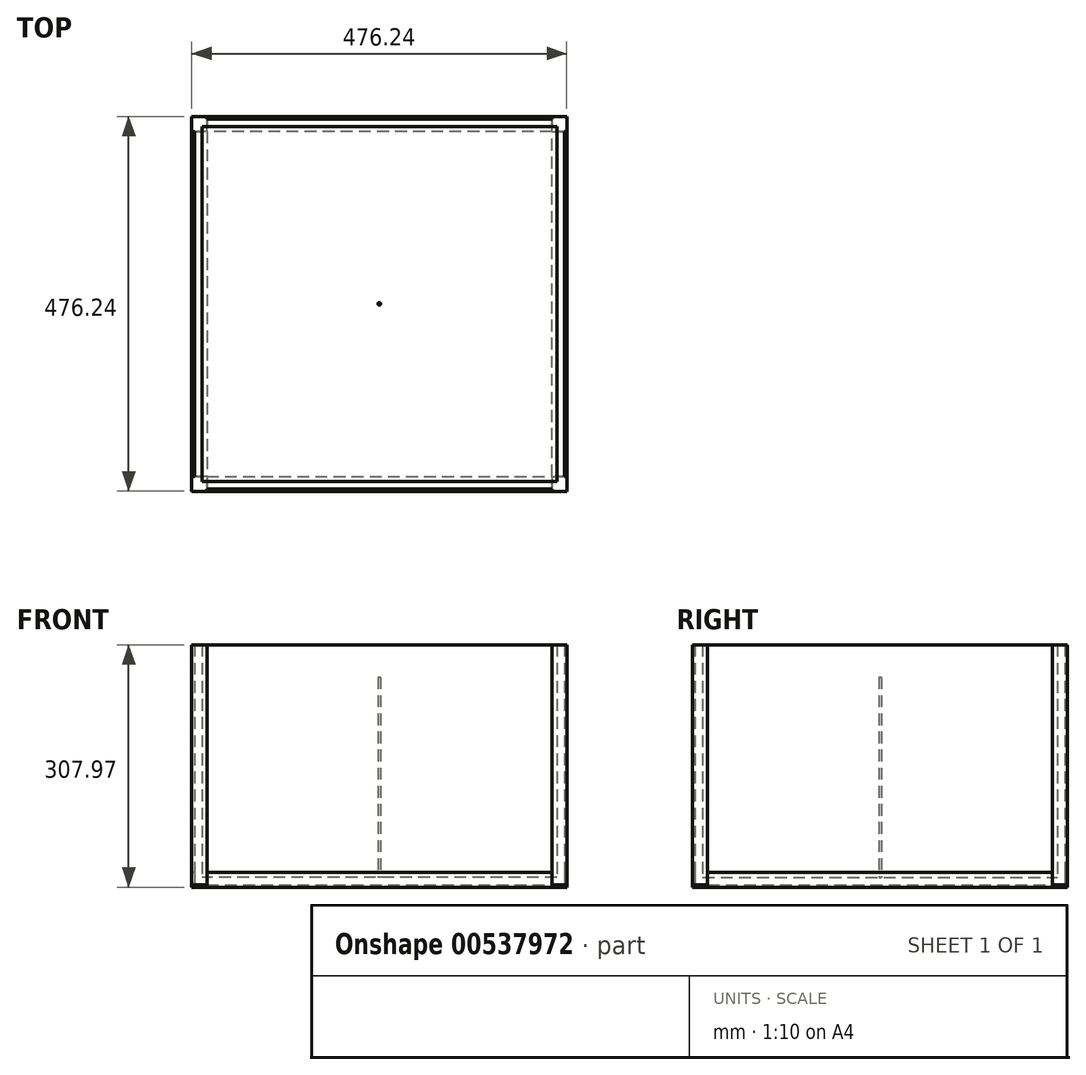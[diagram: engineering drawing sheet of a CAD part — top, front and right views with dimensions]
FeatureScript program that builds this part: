
annotation { "Feature Type Name" : "Feature", "Feature Type Description" : "" }
export const myFeature = defineFeature(function(context is Context, id is Id, definition is map)
    precondition{}
    {
        {
            var Q0;
            Q0=qCreatedBy(makeId("Top.planeOp"),FACE);
            var sketch = newSketch(context, id + "F0", { "sketchPlane" : qUnion([Q0])});
            skLineSegment(sketch, "E0.bottom", {"start": v(234.95, -234.95) * mm, "end": v(-234.95, -234.95) * mm});
            skLineSegment(sketch, "E0.top", {"start": v(234.95, 234.95) * mm, "end": v(-234.95, 234.95) * mm});
            skLineSegment(sketch, "E0.left", {"start": v(234.95, -234.95) * mm, "end": v(234.95, 234.95) * mm});
            skLineSegment(sketch, "E0.right", {"start": v(-234.95, -234.95) * mm, "end": v(-234.95, 234.95) * mm});
            skPoint(sketch, "E0.middle", {"position": v(0, 0) * mm});
            skLineSegment(sketch, "E1", {"start": v(-234.95, 234.95) * mm, "end": v(-234.95, 238.13) * mm});
            skLineSegment(sketch, "E2", {"start": v(-234.95, 238.13) * mm, "end": v(-238.13, 238.13) * mm});
            skLineSegment(sketch, "E3", {"start": v(-238.13, 238.13) * mm, "end": v(-238.13, 219.08) * mm});
            skLineSegment(sketch, "E4", {"start": v(-238.13, 219.08) * mm, "end": v(-234.95, 219.08) * mm});
            skLineSegment(sketch, "E5", {"start": v(-238.13, 238.13) * mm, "end": v(-219.08, 238.13) * mm});
            skLineSegment(sketch, "E6", {"start": v(-219.08, 238.13) * mm, "end": v(-219.08, 234.95) * mm});
            skLineSegment(sketch, "E7.1.0", {"start": v(-238.13, -238.13) * mm, "end": v(-219.08, -238.13) * mm});
            skLineSegment(sketch, "E7.1.1", {"start": v(-219.08, -238.13) * mm, "end": v(-219.08, -234.95) * mm});
            skLineSegment(sketch, "E7.1.2", {"start": v(-238.13, -238.13) * mm, "end": v(-238.13, -219.08) * mm});
            skLineSegment(sketch, "E7.1.3", {"start": v(-238.13, -219.08) * mm, "end": v(-234.95, -219.08) * mm});
            skLineSegment(sketch, "E7.1.4", {"start": v(-238.13, -234.95) * mm, "end": v(-238.13, -238.13) * mm});
            skLineSegment(sketch, "E7.1.5", {"start": v(-234.95, -234.95) * mm, "end": v(-238.13, -234.95) * mm});
            skLineSegment(sketch, "E7.2.0", {"start": v(238.13, -238.13) * mm, "end": v(238.13, -219.08) * mm});
            skLineSegment(sketch, "E7.2.1", {"start": v(238.13, -219.08) * mm, "end": v(234.95, -219.08) * mm});
            skLineSegment(sketch, "E7.2.2", {"start": v(238.13, -238.13) * mm, "end": v(219.08, -238.13) * mm});
            skLineSegment(sketch, "E7.2.3", {"start": v(219.08, -238.13) * mm, "end": v(219.08, -234.95) * mm});
            skLineSegment(sketch, "E7.2.4", {"start": v(234.95, -238.13) * mm, "end": v(238.13, -238.13) * mm});
            skLineSegment(sketch, "E7.2.5", {"start": v(234.95, -234.95) * mm, "end": v(234.95, -238.13) * mm});
            skLineSegment(sketch, "E7.3.0", {"start": v(238.13, 238.13) * mm, "end": v(219.08, 238.13) * mm});
            skLineSegment(sketch, "E7.3.1", {"start": v(219.08, 238.13) * mm, "end": v(219.08, 234.95) * mm});
            skLineSegment(sketch, "E7.3.2", {"start": v(238.13, 238.13) * mm, "end": v(238.13, 219.08) * mm});
            skLineSegment(sketch, "E7.3.3", {"start": v(238.13, 219.08) * mm, "end": v(234.95, 219.08) * mm});
            skLineSegment(sketch, "E7.3.4", {"start": v(238.13, 234.95) * mm, "end": v(238.13, 238.13) * mm});
            skLineSegment(sketch, "E7.3.5", {"start": v(234.95, 234.95) * mm, "end": v(238.13, 234.95) * mm});
            skLineSegment(sketch, "E8.0", {"start": v(225.42, 225.43) * mm, "end": v(-225.43, 225.43) * mm});
            skLineSegment(sketch, "E8.1", {"start": v(225.43, -225.42) * mm, "end": v(225.42, 225.43) * mm});
            skLineSegment(sketch, "E8.2", {"start": v(225.43, -225.42) * mm, "end": v(-225.42, -225.42) * mm});
            skLineSegment(sketch, "E8.3", {"start": v(-225.42, -225.42) * mm, "end": v(-225.43, 225.43) * mm});
            skSolve(sketch);
        }
        {
            var Q0;
            Q0 = qSketchRegion(id + "F0", true);
            extrude(context, id + "F1", {"entities" : qUnion([Q0]), "depth" : 304.8 * mm, "offsetDistance" : 25.4 * mm});
        }
        {
            var Q0;
            Q0=makeQuery(id+"F0.imprint","IMPRINT",FACE,{"disambiguationData":[TD([[makeQuery(id+"F0.imprint","IMPRINT",EDGE,{"derivedFrom":sQuery(id+"F0.wireOp",EDGE,"E8.0")}),1.0]])]});
            extrude(context, id + "F2", {"entities" : qUnion([Q0]), "operationType" : NewBodyOperationType.ADD, "depth" : 9.52 * mm, "offsetDistance" : 25.4 * mm});
        }
        {
            var Q0;
            Q0=makeQuery(id+"F1.opExtrude","SWEPT_FACE",FACE,{"disambiguationData":[OSD([sQuery(id+"F0.wireOp",EDGE,"E7.2.3")])]});
            var sketch = newSketch(context, id + "F3", { "sketchPlane" : qUnion([Q0])});
            skLineSegment(sketch, "E9", {"start": v(234.95, 0) * mm, "end": v(234.95, 15.88) * mm});
            skLineSegment(sketch, "E10", {"start": v(234.95, 15.88) * mm, "end": v(238.12, 15.88) * mm});
            skLineSegment(sketch, "E11", {"start": v(238.12, 15.88) * mm, "end": v(238.12, -3.18) * mm});
            skLineSegment(sketch, "E12", {"start": v(238.12, -3.18) * mm, "end": v(219.07, -3.18) * mm});
            skLineSegment(sketch, "E13", {"start": v(219.07, -3.18) * mm, "end": v(219.07, 0) * mm});
            skLineSegment(sketch, "E14", {"start": v(219.07, 0) * mm, "end": v(234.95, 0) * mm});
            skSolve(sketch);
        }
        {
            var Q0;
            Q0 = qSketchRegion(id + "F3", true);
            var Q1;
            Q1=makeQuery(id+"F1.opExtrude","SWEPT_FACE",FACE,{"disambiguationData":[OSD([sQuery(id+"F0.wireOp",EDGE,"E7.1.1")])]});
            extrude(context, id + "F4", {"entities" : qUnion([Q0]), "endBound" : BoundingType.UP_TO_SURFACE, "depth" : 25.4 * mm, "endBoundEntityFace" : qUnion([Q1]), "offsetDistance" : 25.4 * mm});
        }
        {
            var Q0;
            Q0=makeQuery(id+"F2.opExtrude","CAP_FACE",FACE,{"disambiguationData":[OSD([sQuery(id+"F0.wireOp",EDGE,"E8.0"),sQuery(id+"F0.wireOp",EDGE,"E8.1"),sQuery(id+"F0.wireOp",EDGE,"E8.2"),sQuery(id+"F0.wireOp",EDGE,"E8.3")])],"isStart":false});
            var sketch = newSketch(context, id + "F5", { "sketchPlane" : qUnion([Q0])});
            skCircle(sketch, "E15", {"center": v(0, 0) * mm, "radius": 1.59 * mm});
            skSolve(sketch);
        }
        {
            var Q0;
            Q0 = qSketchRegion(id + "F5", true);
            extrude(context, id + "F6", {"entities" : qUnion([Q0]), "operationType" : NewBodyOperationType.ADD, "depth" : 254 * mm, "offsetDistance" : 25.4 * mm});
        }
        {
            var Q0;
            Q0=makeQuery(id+"F4.opExtrude","SWEPT_BODY",BODY,{"disambiguationData":[OSD([sQuery(id+"F3.wireOp",EDGE,"E9"),sQuery(id+"F3.wireOp",EDGE,"E10"),sQuery(id+"F3.wireOp",EDGE,"E11"),sQuery(id+"F3.wireOp",EDGE,"E12"),sQuery(id+"F3.wireOp",EDGE,"E13"),sQuery(id+"F3.wireOp",EDGE,"E14")])]});
            var Q1;
            Q1=makeQuery(id+"F6.opExtrude","SWEPT_FACE",FACE,{"disambiguationData":[OSD([sQuery(id+"F5.wireOp",EDGE,"E15")])]});
            circularPattern(context, id + "F7", {"entities" : qUnion([Q0]), "axis" : qUnion([Q1]), "angle" : 360 * degree, "instanceCount" : 4, "equalSpace" : true});
        }
    });
